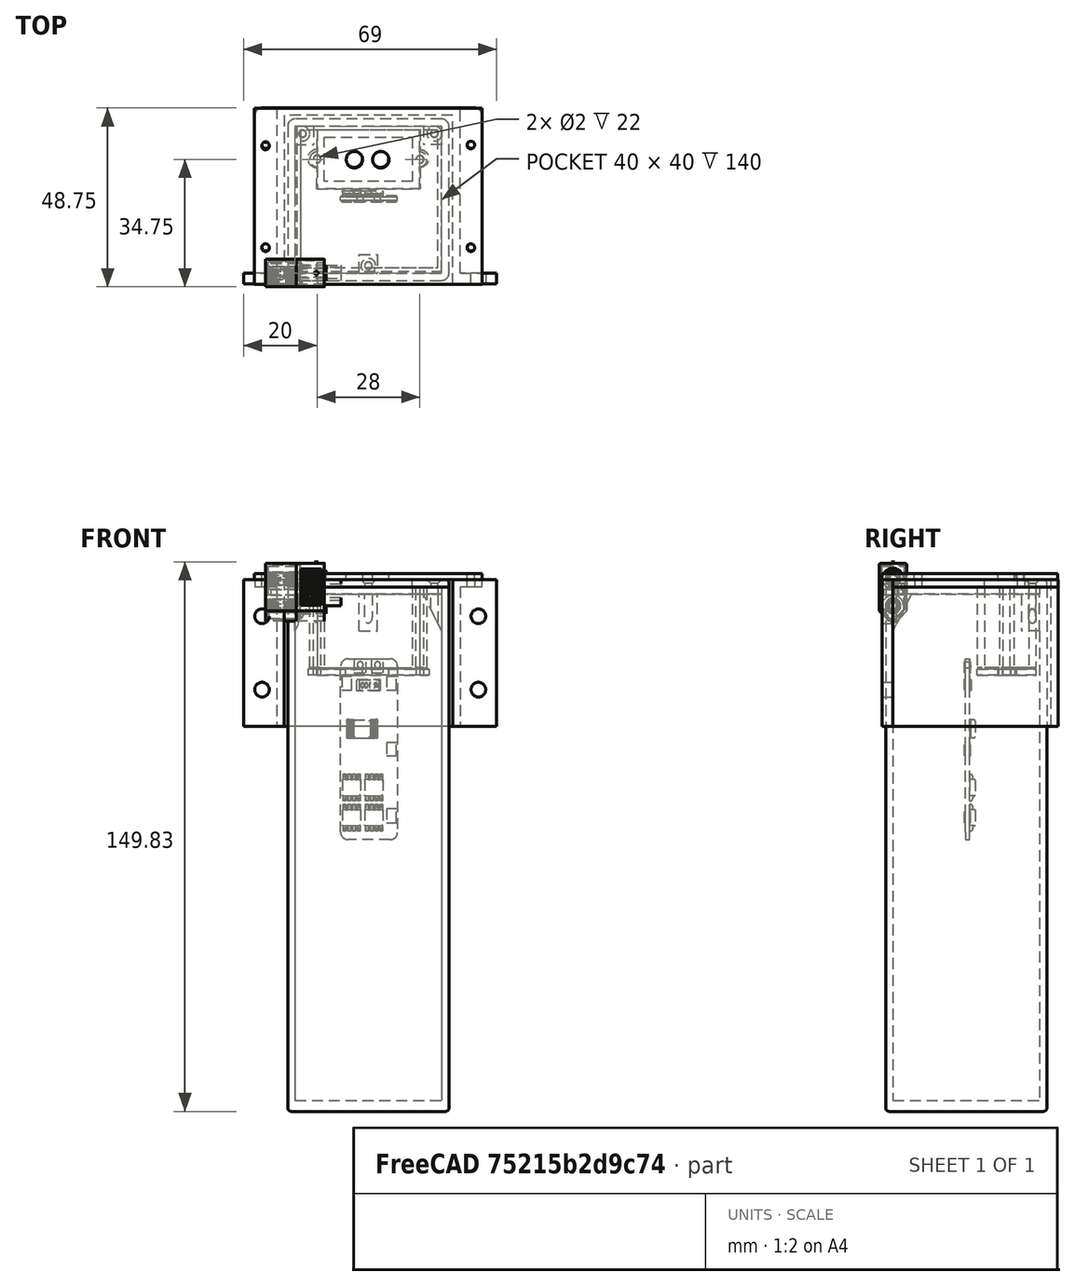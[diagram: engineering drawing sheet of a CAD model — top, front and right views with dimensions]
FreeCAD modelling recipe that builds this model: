
FCSTD DOCUMENT  (FreeCAD 0.20R29177 (Git))
Label: modular_battery_freecad
License: All rights reserved
LicenseURL: http://en.wikipedia.org/wiki/All_rights_reserved
objects: Sketcher::SketchObject×12, Part::Extrusion×11, Part::Feature×9, Part::MultiFuse×7, Mesh::Feature×6, Part::Fillet×3, App::DocumentObjectGroup×3, Part::Compound2×2, Part::Cut×1, Part::Chamfer×1
note: 44 computed .brp shape members not serialized (recipe doc carries the construction recipe); baked Part::Feature solids carry a one-line shape summary decoded from their .brp

FEATURE [Sketcher::SketchObject] Sketch  label="laterales"
  FullyConstrained = true
  sketch-geometry (12):
    g0: LineSegment StartX=0 StartY=0 StartZ=0 EndX=40 EndY=0 EndZ=0
    g1: LineSegment StartX=40 StartY=0 StartZ=0 EndX=40 EndY=40 EndZ=0
    g2: LineSegment StartX=40 StartY=40 StartZ=0 EndX=0 EndY=40 EndZ=0
    g3: LineSegment StartX=0 StartY=40 StartZ=0 EndX=0 EndY=0 EndZ=0
    g4: LineSegment StartX=-4e-16 StartY=-2 StartZ=0 EndX=40 EndY=-2 EndZ=0
    g5: LineSegment StartX=42 StartY=-5e-16 StartZ=0 EndX=42 EndY=40 EndZ=0
    g6: LineSegment StartX=40 StartY=42 StartZ=0 EndX=0 EndY=42 EndZ=0
    g7: LineSegment StartX=-2 StartY=40 StartZ=0 EndX=-2 EndY=0 EndZ=0
    g8: ArcOfCircle CenterX=40 CenterY=40 CenterZ=0 NormalX=0 NormalY=0 NormalZ=1 AngleXU=0 Radius=2 StartAngle=-9e-16 EndAngle=1.5708
    g9: ArcOfCircle CenterX=0 CenterY=40 CenterZ=0 NormalX=0 NormalY=0 NormalZ=1 AngleXU=0 Radius=2 StartAngle=1.5708 EndAngle=3.14159
    g10: ArcOfCircle CenterX=0 CenterY=0 CenterZ=0 NormalX=0 NormalY=0 NormalZ=1 AngleXU=0 Radius=2 StartAngle=3.14159 EndAngle=4.71239
    g11: ArcOfCircle CenterX=40 CenterY=0 CenterZ=0 NormalX=0 NormalY=0 NormalZ=1 AngleXU=0 Radius=2 StartAngle=4.71239 EndAngle=6.28319
  constraints (28):
    c: Coincident(g0,g1)
    c: Coincident(g1,g2)
    c: Coincident(g2,g3)
    c: Coincident(g3,g0)
    c: Horizontal(g0)
    c: Horizontal(g2)
    c: Vertical(g1)
    c: Vertical(g3)
    c: Coincident(g0,g-1)
    c: DistanceX(g2,g2) = 40
    c: DistanceY(g3,g3) = 40
    c: Horizontal(g4)
    c: Horizontal(g6)
    c: Vertical(g5)
    c: Vertical(g7)
    c: Tangent(g5,g8) = -1.5708
    c: Tangent(g6,g8) = -1.5708
    c: Radius(g8) = 2
    c: DistanceX(g1,g5) = 2
    c: Tangent(g6,g9) = -1.5708
    c: Tangent(g7,g9) = -1.5708
    c: Tangent(g4,g10) = -1.5708
    c: Tangent(g7,g10) = -1.5708
    c: Tangent(g4,g11) = -1.5708
    c: Tangent(g5,g11) = -1.5708
    c: Coincident(g11,g0)
    c: Coincident(g10,g0)
    c: Coincident(g2,g9)
FEATURE [Mesh::Feature] _8650_Refrence_Cell  label="18650_Refrence_Cell"
  Placement = pos=(270.809,20.8001,-137.861) rot=(0,0,1;0rad)
FEATURE [Mesh::Feature] _8650_Refrence_Cell001  label="18650_Refrence_Cell001"
  Placement = pos=(249.245,20.7563,-137.861) rot=(0,0,1;0rad)
FEATURE [Mesh::Feature] _8650_Refrence_Cell002  label="18650_Refrence_Cell002"
  Placement = pos=(270.809,-0.622475,-137.861) rot=(0,0,1;0rad)
FEATURE [Mesh::Feature] _8650_Refrence_Cell003  label="18650_Refrence_Cell003"
  Placement = pos=(249.245,-0.66626,-137.861) rot=(0,0,1;0rad)
FEATURE [Mesh::Feature] _8650_Refrence_Cell004  label="18650_Refrence_Cell004"
  Placement = pos=(270.809,-0.622475,-71.3701) rot=(0,0,1;0rad)
FEATURE [Mesh::Feature] _8650_Refrence_Cell005  label="18650_Refrence_Cell005"
  Placement = pos=(249.245,-0.66626,-71.3701) rot=(0,0,1;0rad)
FEATURE [Part::Feature] Solid
  shape: bbox 19.85 x 5.084 x 5.084 mm, 17 faces (baked)
FEATURE [Part::Feature] Solid001
  shape: bbox 19.85 x 5.084 x 5.084 mm, 17 faces (baked)
FEATURE [Part::Feature] Solid002
  shape: bbox 15.7 x 7.5 x 16.55 mm, 359 faces (baked)
FEATURE [Part::Compound2] Compound  label="XT60MaleConnector"
  Links = -> [Solid,Solid001,Solid002]
  Placement = pos=(21.25,31.08,-13.9) rot=(0,1,0;1.5708rad)
FEATURE [Part::Feature] Solid003  label="3PCS BMS Charger Module 12V 10A 18650 Lithium Battery"
  Placement = pos=(20.2003,19.7527,-44.2521) rot=(0,1,0;1.5708rad)
  shape: bbox 15.5 x 2.96 x 49.3 mm, 384 faces (baked)
FEATURE [Part::Extrusion] Extrude  label="laterales001"
  Base = -> Sketch
  Dir = (0,0,1)
  DirMode = 2
  FaceMakerClass = Part::FaceMakerBullseye
  LengthFwd = -140
  LengthRev = 0
  Solid = true
  Symmetric = false
FEATURE [Sketcher::SketchObject] Sketch001  label="base"
  FullyConstrained = true
  Placement = pos=(0,0,-140) rot=(0,0,1;0rad)
  sketch-geometry (8):
    g0: LineSegment StartX=-4e-16 StartY=-2 StartZ=0 EndX=40 EndY=-2 EndZ=0
    g1: LineSegment StartX=42 StartY=-5e-16 StartZ=0 EndX=42 EndY=40 EndZ=0
    g2: LineSegment StartX=40 StartY=42 StartZ=0 EndX=0 EndY=42 EndZ=0
    g3: LineSegment StartX=-2 StartY=40 StartZ=0 EndX=-2 EndY=0 EndZ=0
    g4: ArcOfCircle CenterX=40 CenterY=40 CenterZ=0 NormalX=0 NormalY=0 NormalZ=1 AngleXU=0 Radius=2 StartAngle=-9e-16 EndAngle=1.5708
    g5: ArcOfCircle CenterX=0 CenterY=40 CenterZ=0 NormalX=0 NormalY=0 NormalZ=1 AngleXU=0 Radius=2 StartAngle=1.5708 EndAngle=3.14159
    g6: ArcOfCircle CenterX=0 CenterY=0 CenterZ=0 NormalX=0 NormalY=0 NormalZ=1 AngleXU=0 Radius=2 StartAngle=3.14159 EndAngle=4.71239
    g7: ArcOfCircle CenterX=40 CenterY=0 CenterZ=0 NormalX=0 NormalY=0 NormalZ=1 AngleXU=0 Radius=2 StartAngle=4.71239 EndAngle=6.28319
  constraints (19):
    c: Horizontal(g0)
    c: Horizontal(g2)
    c: Vertical(g1)
    c: Vertical(g3)
    c: Tangent(g1,g4) = -1.5708
    c: Tangent(g2,g4) = -1.5708
    c: Radius(g4) = 2
    c: Tangent(g2,g5) = -1.5708
    c: Tangent(g3,g5) = -1.5708
    c: Tangent(g0,g6) = -1.5708
    c: Tangent(g3,g6) = -1.5708
    c: Tangent(g0,g7) = -1.5708
    c: Tangent(g1,g7) = -1.5708
    c: Radius(g5) = 2
    c: Radius(g7) = 2
    c: Radius(g6) = 2
    c: DistanceX(g2,g2) = 40
    c: DistanceY(g0,g2) = 44
    c: Coincident(g6,g-1)
FEATURE [Part::Extrusion] Extrude001
  Base = -> Sketch001
  Dir = (0,0,1)
  DirMode = 2
  FaceMakerClass = Part::FaceMakerBullseye
  LengthFwd = -3
  LengthRev = 0
  Solid = true
  Symmetric = false
FEATURE [Part::Fillet] Fillet
  Base = -> Extrude001
  Edges = 3 edges r=1: [Edge16,Edge19,Edge22]
FEATURE [Sketcher::SketchObject] Sketch003  label="base002"
  FullyConstrained = true
  sketch-geometry (15):
    g0: LineSegment StartX=-4e-16 StartY=-2 StartZ=0 EndX=40 EndY=-2 EndZ=0
    g1: LineSegment StartX=42 StartY=3.4e-15 StartZ=0 EndX=42 EndY=40 EndZ=0
    g2: LineSegment StartX=40 StartY=42 StartZ=0 EndX=0 EndY=42 EndZ=0
    g3: LineSegment StartX=-2 StartY=40 StartZ=0 EndX=-2 EndY=0 EndZ=0
    g4: ArcOfCircle CenterX=40 CenterY=40 CenterZ=0 NormalX=0 NormalY=0 NormalZ=1 AngleXU=0 Radius=2 StartAngle=-9e-16 EndAngle=1.5708
    g5: ArcOfCircle CenterX=0 CenterY=40 CenterZ=0 NormalX=0 NormalY=0 NormalZ=1 AngleXU=0 Radius=2 StartAngle=1.5708 EndAngle=3.14159
    g6: ArcOfCircle CenterX=0 CenterY=0 CenterZ=0 NormalX=0 NormalY=0 NormalZ=1 AngleXU=0 Radius=2 StartAngle=3.14159 EndAngle=4.71239
    g7: ArcOfCircle CenterX=40 CenterY=3.9e-15 CenterZ=0 NormalX=0 NormalY=0 NormalZ=1 AngleXU=0 Radius=2 StartAngle=4.71239 EndAngle=6.28319
    g8: Circle CenterX=2 CenterY=38 CenterZ=0 NormalX=0 NormalY=0 NormalZ=1 AngleXU=0 Radius=1
    g9: Circle CenterX=38 CenterY=38 CenterZ=0 NormalX=0 NormalY=0 NormalZ=1 AngleXU=0 Radius=1
    g10: Circle CenterX=20 CenterY=2 CenterZ=0 NormalX=0 NormalY=0 NormalZ=1 AngleXU=0 Radius=1
    g11: LineSegment StartX=8 StartY=37 StartZ=0 EndX=32 EndY=37 EndZ=0
    g12: LineSegment StartX=32 StartY=37 StartZ=0 EndX=32 EndY=25 EndZ=0
    g13: LineSegment StartX=32 StartY=25 StartZ=0 EndX=8 EndY=25 EndZ=0
    g14: LineSegment StartX=8 StartY=25 StartZ=0 EndX=8 EndY=37 EndZ=0
  constraints (40):
    c: Horizontal(g0)
    c: Horizontal(g2)
    c: Vertical(g1)
    c: Vertical(g3)
    c: Tangent(g1,g4) = -1.5708
    c: Tangent(g2,g4) = -1.5708
    c: Radius(g4) = 2
    c: Tangent(g2,g5) = -1.5708
    c: Tangent(g3,g5) = -1.5708
    c: Tangent(g0,g6) = -1.5708
    c: Tangent(g3,g6) = -1.5708
    c: Tangent(g0,g7) = -1.5708
    c: Tangent(g1,g7) = -1.5708
    c: Diameter(g8) = 2
    c: Equal(g10,g9)
    c: Equal(g9,g8)
    c: DistanceY(g7,g10) = 2
    c: DistanceX(g10,g7) = 20
    c: DistanceY(g8,g5) = 2
    c: DistanceX(g5,g8) = 2
    c: Radius(g5) = 2
    c: DistanceX(g9,g4) = 2
    c: DistanceY(g9,g4) = 2
    c: Radius(g7) = 2
    c: Radius(g6) = 2
    c: DistanceX(g2,g2) = 40
    c: DistanceY(g0,g2) = 44
    c: Coincident(g6,g-1)
    c: Coincident(g11,g12)
    c: Coincident(g12,g13)
    c: Coincident(g13,g14)
    c: Coincident(g14,g11)
    c: Horizontal(g11)
    c: Horizontal(g13)
    c: Vertical(g12)
    c: Vertical(g14)
    c: DistanceX(g11,g1) = 10
    c: DistanceX(g3,g11) = 10
    c: DistanceY(g11,g2) = 5
    c: DistanceY(g0,g12) = 27
FEATURE [Sketcher::SketchObject] Sketch004  label="base003"
  FullyConstrained = false
  sketch-geometry (14):
    g0: LineSegment StartX=8 StartY=37 StartZ=0 EndX=32 EndY=37 EndZ=0
    g1: LineSegment StartX=32 StartY=37 StartZ=0 EndX=32 EndY=25 EndZ=0
    g2: LineSegment StartX=32 StartY=25 StartZ=0 EndX=8 EndY=25 EndZ=0
    g3: LineSegment StartX=8 StartY=25 StartZ=0 EndX=8 EndY=37 EndZ=0
    g4: LineSegment StartX=34 StartY=39 StartZ=0 EndX=6 EndY=39 EndZ=0
    g5: LineSegment StartX=6 StartY=39 StartZ=0 EndX=6 EndY=33 EndZ=0
    g6: LineSegment StartX=6 StartY=23 StartZ=0 EndX=34 EndY=23 EndZ=0
    g7: LineSegment StartX=34 StartY=23 StartZ=0 EndX=34 EndY=29 EndZ=0
    g8: Circle CenterX=6 CenterY=31 CenterZ=0 NormalX=0 NormalY=0 NormalZ=1 AngleXU=0 Radius=1
    g9: ArcOfCircle CenterX=6 CenterY=31 CenterZ=0 NormalX=0 NormalY=0 NormalZ=1 AngleXU=0 Radius=2 StartAngle=1.5708 EndAngle=4.71239
    g10: LineSegment StartX=6 StartY=29 StartZ=0 EndX=6 EndY=23 EndZ=0
    g11: Circle CenterX=34 CenterY=31 CenterZ=0 NormalX=0 NormalY=0 NormalZ=1 AngleXU=0 Radius=1
    g12: ArcOfCircle CenterX=34 CenterY=31 CenterZ=0 NormalX=0 NormalY=0 NormalZ=1 AngleXU=0 Radius=2 StartAngle=4.71239 EndAngle=7.85398
    g13: LineSegment StartX=34 StartY=33 StartZ=0 EndX=34 EndY=39 EndZ=0
  constraints (42):
    c: Coincident(g0,g1)
    c: Coincident(g1,g2)
    c: Coincident(g2,g3)
    c: Coincident(g3,g0)
    c: Horizontal(g0)
    c: Horizontal(g2)
    c: Vertical(g1)
    c: Vertical(g3)
    c: DistanceY(g-1,g2) = 25
    c: DistanceX(g-1,g2) = 8
    c: DistanceX(g0,g0) = 24
    c: DistanceY(g1,g1) = 12
    c: Coincident(g4,g5)
    c: Coincident(g10,g6)
    c: Coincident(g6,g7)
    c: Coincident(g13,g4)
    c: Horizontal(g4)
    c: Horizontal(g6)
    c: Vertical(g5)
    c: Vertical(g7)
    c: DistanceY(g10,g2) = 2
    c: DistanceX(g10,g2) = 2
    c: DistanceX(g6,g6) = 28
    c: PointOnObject(g8,g5)
    c: Coincident(g9,g8)
    c: Diameter(g8) = 2
    c: Diameter(g9) = 4
    c: Coincident(g5,g9)
    c: Coincident(g9,g10)
    c: PointOnObject(g11,g7)
    c: Coincident(g12,g11)
    c: Diameter(g11) = 2
    c: Diameter(g12) = 4
    c: PointOnObject(g12,g7)
    c: Coincident(g7,g12)
    c: PointOnObject(g13,g12)
    c: DistanceY(g6,g4) = 16
    c: Vertical(g13)
    c: DistanceY(g6,g11) = 8
    c: DistanceY(g6,g8) = 8
    c: Vertical(g10)
    c: DistanceX(g5,g0) = 2
FEATURE [Sketcher::SketchObject] Sketch005  label="base004"
  FullyConstrained = true
  sketch-geometry (8):
    g0: LineSegment StartX=8 StartY=37 StartZ=0 EndX=32 EndY=37 EndZ=0
    g1: LineSegment StartX=32 StartY=37 StartZ=0 EndX=32 EndY=25 EndZ=0
    g2: LineSegment StartX=32 StartY=25 StartZ=0 EndX=8 EndY=25 EndZ=0
    g3: LineSegment StartX=8 StartY=25 StartZ=0 EndX=8 EndY=37 EndZ=0
    g4: LineSegment StartX=6 StartY=39 StartZ=0 EndX=34 EndY=39 EndZ=0
    g5: LineSegment StartX=34 StartY=39 StartZ=0 EndX=34 EndY=23 EndZ=0
    g6: LineSegment StartX=34 StartY=23 StartZ=0 EndX=6 EndY=23 EndZ=0
    g7: LineSegment StartX=6 StartY=23 StartZ=0 EndX=6 EndY=39 EndZ=0
  constraints (24):
    c: Coincident(g0,g1)
    c: Coincident(g1,g2)
    c: Coincident(g2,g3)
    c: Coincident(g3,g0)
    c: Horizontal(g0)
    c: Horizontal(g2)
    c: Vertical(g1)
    c: Vertical(g3)
    c: DistanceY(g-1,g2) = 25
    c: DistanceX(g-1,g2) = 8
    c: DistanceX(g0,g0) = 24
    c: DistanceY(g1,g1) = 12
    c: Coincident(g4,g5)
    c: Coincident(g5,g6)
    c: Coincident(g6,g7)
    c: Coincident(g7,g4)
    c: Horizontal(g4)
    c: Horizontal(g6)
    c: Vertical(g5)
    c: Vertical(g7)
    c: DistanceX(g1,g5) = 2
    c: DistanceY(g5,g1) = 2
    c: DistanceY(g5,g5) = 16
    c: DistanceX(g4,g4) = 28
FEATURE [Part::Extrusion] Extrude002
  Base = -> Sketch003
  Dir = (0,0,1)
  DirMode = 2
  FaceMakerClass = Part::FaceMakerBullseye
  LengthFwd = 2
  LengthRev = 0
  Solid = true
  Symmetric = false
FEATURE [Part::Extrusion] Extrude003
  Base = -> Sketch004
  Dir = (0,0,1)
  DirMode = 2
  FaceMakerClass = Part::FaceMakerBullseye
  LengthFwd = -22
  LengthRev = 0
  Solid = true
  Symmetric = false
FEATURE [Part::Feature] Solid004
  shape: bbox 19.85 x 5.085 x 5.085 mm, 36 faces (baked)
FEATURE [Part::Feature] Solid005
  shape: bbox 19.85 x 5.085 x 5.085 mm, 36 faces (baked)
FEATURE [Part::Feature] Solid006
  shape: bbox 16 x 7.5 x 16.55 mm, 345 faces (baked)
FEATURE [Part::Compound2] Compound001  label="XT60FemaleConnector"
  Links = -> [Solid004,Solid005,Solid006]
  Placement = pos=(21.25,31.04,-6) rot=(0.707107,0,0.707107;3.14159rad)
FEATURE [Part::Fillet] Fillet001
  Base = -> Extrude002
  Edges = 1 edges r=1: [Edge16]
FEATURE [Part::MultiFuse] Fusion
  Shapes = -> [Extrude,Fillet]
FEATURE [Sketcher::SketchObject] Sketch006  label="base005"
  FullyConstrained = true
  sketch-geometry (8):
    g0: LineSegment StartX=0.5 StartY=0.5 StartZ=0 EndX=40 EndY=0.5 EndZ=0
    g1: LineSegment StartX=40 StartY=0.5 StartZ=0 EndX=40 EndY=40 EndZ=0
    g2: LineSegment StartX=40 StartY=40 StartZ=0 EndX=0.5 EndY=40 EndZ=0
    g3: LineSegment StartX=0.5 StartY=40 StartZ=0 EndX=0.5 EndY=0.5 EndZ=0
    g4: LineSegment StartX=39 StartY=39 StartZ=0 EndX=1.5 EndY=39 EndZ=0
    g5: LineSegment StartX=1.5 StartY=39 StartZ=0 EndX=1.5 EndY=1.5 EndZ=0
    g6: LineSegment StartX=1.5 StartY=1.5 StartZ=0 EndX=39 EndY=1.5 EndZ=0
    g7: LineSegment StartX=39 StartY=1.5 StartZ=0 EndX=39 EndY=39 EndZ=0
  constraints (24):
    c: Coincident(g0,g1)
    c: Coincident(g1,g2)
    c: Coincident(g2,g3)
    c: Horizontal(g0)
    c: Horizontal(g2)
    c: Vertical(g1)
    c: Vertical(g3)
    c: DistanceY(g1,g1) = 39.5
    c: DistanceX(g0,g0) = 39.5
    c: Coincident(g0,g3)
    c: DistanceX(g-1,g0) = 0.5
    c: DistanceY(g-1,g0) = 0.5
    c: Coincident(g4,g5)
    c: Coincident(g5,g6)
    c: Coincident(g6,g7)
    c: Coincident(g7,g4)
    c: Horizontal(g4)
    c: Horizontal(g6)
    c: Vertical(g5)
    c: Vertical(g7)
    c: DistanceY(g4,g1) = 1
    c: DistanceX(g4,g1) = 1
    c: DistanceX(g4,g4) = 37.5
    c: DistanceY(g7,g7) = 37.5
FEATURE [Part::Extrusion] Extrude004
  Base = -> Sketch006
  Dir = (0,0,1)
  DirMode = 2
  FaceMakerClass = Part::FaceMakerBullseye
  LengthFwd = -2
  LengthRev = 0
  Solid = true
  Symmetric = false
FEATURE [Part::MultiFuse] Fusion001
  Shapes = -> [Fillet001,Extrude004]
FEATURE [Part::MultiFuse] Fusion002
  Shapes = -> [Fusion001,Extrude003]
FEATURE [Sketcher::SketchObject] Sketch008  label="base006"
  FullyConstrained = false
  sketch-geometry (3):
    g0: Circle CenterX=2 CenterY=38 CenterZ=0 NormalX=0 NormalY=0 NormalZ=1 AngleXU=0 Radius=1
    g1: Circle CenterX=38 CenterY=38 CenterZ=0 NormalX=0 NormalY=0 NormalZ=1 AngleXU=0 Radius=1
    g2: Circle CenterX=20 CenterY=2 CenterZ=0 NormalX=0 NormalY=0 NormalZ=1 AngleXU=0 Radius=1
  constraints (2):
    c: Diameter(g0) = 2
    c: Equal(g2,g1)
FEATURE [Sketcher::SketchObject] Sketch007  label="laterales002"
  FullyConstrained = true
  Placement = pos=(0,0,2) rot=(0,0,1;0rad)
  sketch-geometry (8):
    g0: LineSegment StartX=43 StartY=-3 StartZ=0 EndX=43 EndY=43 EndZ=0
    g1: LineSegment StartX=43 StartY=43 StartZ=0 EndX=-3 EndY=43 EndZ=0
    g2: LineSegment StartX=-3 StartY=43 StartZ=0 EndX=-3 EndY=-3 EndZ=0
    g3: LineSegment StartX=45 StartY=-3 StartZ=0 EndX=45 EndY=45 EndZ=0
    g4: LineSegment StartX=45 StartY=45 StartZ=0 EndX=-5 EndY=45 EndZ=0
    g5: LineSegment StartX=-5 StartY=45 StartZ=0 EndX=-5 EndY=-3 EndZ=0
    g6: LineSegment StartX=45 StartY=-3 StartZ=0 EndX=43 EndY=-3 EndZ=0
    g7: LineSegment StartX=-3 StartY=-3 StartZ=0 EndX=-5 EndY=-3 EndZ=0
  constraints (24):
    c: Coincident(g0,g1)
    c: Coincident(g1,g2)
    c: Horizontal(g1)
    c: Vertical(g0)
    c: Vertical(g2)
    c: DistanceX(g1,g1) = 46
    c: DistanceY(g0,g0) = 46
    c: DistanceY(g2,g-1) = 3
    c: DistanceX(g2,g-1) = 3
    c: Coincident(g3,g4)
    c: Coincident(g4,g5)
    c: Horizontal(g4)
    c: Vertical(g3)
    c: Vertical(g5)
    c: DistanceY(g3,g3) = 48
    c: DistanceX(g4,g4) = 50
    c: DistanceY(g1,g4) = 2
    c: Coincident(g6,g3)
    c: Coincident(g6,g0)
    c: DistanceY(g5,g5) = 48
    c: Coincident(g7,g2)
    c: Horizontal(g7)
    c: Coincident(g5,g7)
    c: DistanceX(g7,g7) = 2
FEATURE [Sketcher::SketchObject] Sketch009
  FullyConstrained = true
  Placement = pos=(0,40,0) rot=(1,0,0;1.5708rad)
  sketch-geometry (6):
    g0: LineSegment StartX=0 StartY=0 StartZ=0 EndX=5 EndY=0 EndZ=0
    g1: LineSegment StartX=5 StartY=0 StartZ=0 EndX=0 EndY=-10 EndZ=0
    g2: LineSegment StartX=0 StartY=-10 StartZ=0 EndX=0 EndY=0 EndZ=0
    g3: LineSegment StartX=40 StartY=0 StartZ=0 EndX=35 EndY=0 EndZ=0
    g4: LineSegment StartX=40 StartY=0 StartZ=0 EndX=40 EndY=-10 EndZ=0
    g5: LineSegment StartX=40 StartY=-10 StartZ=0 EndX=35 EndY=0 EndZ=0
  constraints (17):
    c: Coincident(g0,g-1)
    c: Horizontal(g0)
    c: Coincident(g1,g0)
    c: PointOnObject(g1,g-2)
    c: Coincident(g2,g1)
    c: Coincident(g2,g0)
    c: DistanceY(g2,g2) = 10
    c: DistanceX(g0,g0) = 5
    c: PointOnObject(g3,g-1)
    c: PointOnObject(g3,g-1)
    c: DistanceX(g0,g3) = 40
    c: DistanceX(g3,g3) = 5
    c: Coincident(g4,g3)
    c: Vertical(g4)
    c: Coincident(g5,g4)
    c: Coincident(g5,g3)
    c: DistanceY(g4,g4) = 10
FEATURE [Part::Extrusion] Extrude005
  Base = -> Sketch009
  Dir = (0,-1,2e-16)
  DirMode = 2
  FaceMakerClass = Part::FaceMakerBullseye
  LengthFwd = 5
  LengthRev = 0
  Solid = true
  Symmetric = false
FEATURE [Sketcher::SketchObject] Sketch010
  FullyConstrained = true
  Placement = pos=(17.5,0,0) rot=(0.57735,0.57735,0.57735;2.0944rad)
  sketch-geometry (3):
    g0: LineSegment StartX=0 StartY=0 StartZ=0 EndX=5 EndY=0 EndZ=0
    g1: LineSegment StartX=5 StartY=0 StartZ=0 EndX=0 EndY=-10 EndZ=0
    g2: LineSegment StartX=0 StartY=-10 StartZ=0 EndX=0 EndY=0 EndZ=0
  constraints (8):
    c: Coincident(g0,g-1)
    c: PointOnObject(g0,g-1)
    c: Coincident(g1,g0)
    c: PointOnObject(g1,g-2)
    c: Coincident(g2,g1)
    c: Coincident(g2,g0)
    c: DistanceX(g0,g0) = 5
    c: DistanceY(g2,g2) = 10
FEATURE [Part::Extrusion] Extrude006
  Base = -> Sketch010
  Dir = (1,-2e-16,2e-16)
  DirMode = 2
  FaceMakerClass = Part::FaceMakerBullseye
  LengthFwd = 5
  LengthRev = 0
  Solid = true
  Symmetric = false
FEATURE [Part::Extrusion] Extrude007
  Base = -> Sketch008
  Dir = (0,0,1)
  DirMode = 2
  FaceMakerClass = Part::FaceMakerBullseye
  LengthFwd = -10
  LengthRev = 0
  Solid = true
  Symmetric = false
FEATURE [Part::MultiFuse] Fusion003
  Shapes = -> [Extrude005,Extrude006]
FEATURE [Part::Cut] Cut
  Base = -> Fusion003
  Placement = pos=(0,0,-2) rot=(0,0,1;0rad)
  Tool = -> Extrude007
FEATURE [Part::Chamfer] Chamfer
  Base = -> Fusion002
  Edges = 3 edges r=1: [Edge96,Edge98,Edge100]
FEATURE [Part::MultiFuse] Fusion004
  Shapes = -> [Cut,Fusion]
FEATURE [Part::Feature] Solid009  label="modular_battery_kicad 1"
  Placement = pos=(6.11,23.06,-24) rot=(0,0,1;0rad)
  shape: bbox 32.96 x 16.2 x 1.6 mm, 15 faces (baked)
FEATURE [App::DocumentObjectGroup] Group  label="vitamins"
  Group = -> [_8650_Refrence_Cell,_8650_Refrence_Cell001,_8650_Refrence_Cell002,_8650_Refrence_Cell003,_8650_Refrence_Cell004,_8650_Refrence_Cell005,Compound,Solid003,Solid009]
FEATURE [Part::Extrusion] Extrude008
  Base = -> Sketch007
  Dir = (0,0,1)
  DirMode = 2
  FaceMakerClass = Part::FaceMakerBullseye
  LengthFwd = -40
  LengthRev = 0
  Solid = true
  Symmetric = false
FEATURE [Sketcher::SketchObject] Sketch011  label="laterales003"
  FullyConstrained = true
  Placement = pos=(0,0,2) rot=(0,0,1;0rad)
  sketch-geometry (12):
    g0: LineSegment StartX=45 StartY=-3 StartZ=0 EndX=51 EndY=-3 EndZ=0
    g1: LineSegment StartX=51 StartY=-3 StartZ=0 EndX=51 EndY=45 EndZ=0
    g2: LineSegment StartX=51 StartY=45 StartZ=0 EndX=45 EndY=45 EndZ=0
    g3: LineSegment StartX=45 StartY=45 StartZ=0 EndX=45 EndY=-3 EndZ=0
    g4: LineSegment StartX=-5 StartY=45 StartZ=0 EndX=-11 EndY=45 EndZ=0
    g5: LineSegment StartX=-11 StartY=45 StartZ=0 EndX=-11 EndY=-3 EndZ=0
    g6: LineSegment StartX=-11 StartY=-3 StartZ=0 EndX=-5 EndY=-3 EndZ=0
    g7: LineSegment StartX=-5 StartY=-3 StartZ=0 EndX=-5 EndY=45 EndZ=0
    g8: Circle CenterX=48 CenterY=35 CenterZ=0 NormalX=0 NormalY=0 NormalZ=1 AngleXU=0 Radius=1
    g9: Circle CenterX=48 CenterY=7 CenterZ=0 NormalX=0 NormalY=0 NormalZ=1 AngleXU=0 Radius=1
    g10: Circle CenterX=-8 CenterY=7 CenterZ=0 NormalX=0 NormalY=0 NormalZ=1 AngleXU=0 Radius=1
    g11: Circle CenterX=-8 CenterY=35 CenterZ=0 NormalX=0 NormalY=0 NormalZ=1 AngleXU=0 Radius=1
  constraints (36):
    c: DistanceY(g0,g2) = 48
    c: DistanceX(g4,g2) = 50
    c: DistanceY(g6,g4) = 48
    c: Coincident(g0,g1)
    c: Coincident(g1,g2)
    c: Coincident(g2,g3)
    c: Coincident(g3,g0)
    c: Horizontal(g0)
    c: Horizontal(g2)
    c: Vertical(g1)
    c: DistanceX(g2,g2) = 6
    c: DistanceY(g-1,g2) = 45
    c: DistanceX(g6,g-1) = 5
    c: DistanceY(g6,g-1) = 3
    c: Coincident(g4,g5)
    c: Coincident(g5,g6)
    c: Coincident(g6,g7)
    c: Coincident(g7,g4)
    c: Horizontal(g4)
    c: Horizontal(g6)
    c: Vertical(g5)
    c: DistanceX(g4,g4) = 6
    c: Equal(g10,g11)
    c: Equal(g11,g8)
    c: Equal(g8,g9)
    c: Diameter(g9) = 2
    c: DistanceX(g0,g9) = 3
    c: DistanceY(g0,g9) = 10
    c: DistanceX(g0,g8) = 3
    c: DistanceY(g8,g2) = 10
    c: DistanceX(g11,g4) = 3
    c: DistanceY(g11,g4) = 10
    c: DistanceX(g10,g6) = 3
    c: DistanceY(g6,g10) = 10
    c: DistanceX(g6,g6) = 6
    c: DistanceX(g0,g0) = 6
FEATURE [Part::Extrusion] Extrude009
  Base = -> Sketch011
  Dir = (0,0,1)
  DirMode = 2
  FaceMakerClass = Part::FaceMakerBullseye
  LengthFwd = -2
  LengthRev = 0
  Solid = true
  Symmetric = false
FEATURE [Sketcher::SketchObject] Sketch012
  FullyConstrained = true
  Placement = pos=(0,0,0) rot=(1,0,0;1.5708rad)
  sketch-geometry (12):
    g0: LineSegment StartX=-4 StartY=2 StartZ=0 EndX=-14 EndY=2 EndZ=0
    g1: LineSegment StartX=-14 StartY=2 StartZ=0 EndX=-14 EndY=-38 EndZ=0
    g2: LineSegment StartX=-14 StartY=-38 StartZ=0 EndX=-4 EndY=-38 EndZ=0
    g3: LineSegment StartX=-4 StartY=-38 StartZ=0 EndX=-4 EndY=2 EndZ=0
    g4: LineSegment StartX=55 StartY=2 StartZ=0 EndX=45 EndY=2 EndZ=0
    g5: LineSegment StartX=45 StartY=2 StartZ=0 EndX=45 EndY=-38 EndZ=0
    g6: LineSegment StartX=45 StartY=-38 StartZ=0 EndX=55 EndY=-38 EndZ=0
    g7: LineSegment StartX=55 StartY=-38 StartZ=0 EndX=55 EndY=2 EndZ=0
    g8: Circle CenterX=-9 CenterY=-8 CenterZ=0 NormalX=0 NormalY=0 NormalZ=1 AngleXU=0 Radius=2
    g9: Circle CenterX=-9 CenterY=-28 CenterZ=0 NormalX=0 NormalY=0 NormalZ=1 AngleXU=0 Radius=2
    g10: Circle CenterX=50 CenterY=-8 CenterZ=0 NormalX=0 NormalY=0 NormalZ=1 AngleXU=0 Radius=2
    g11: Circle CenterX=50 CenterY=-28 CenterZ=0 NormalX=0 NormalY=0 NormalZ=1 AngleXU=0 Radius=2
  constraints (36):
    c: Coincident(g0,g1)
    c: Coincident(g1,g2)
    c: Coincident(g2,g3)
    c: Coincident(g3,g0)
    c: Horizontal(g0)
    c: Horizontal(g2)
    c: Vertical(g1)
    c: Vertical(g3)
    c: DistanceX(g2,g2) = 10
    c: DistanceY(g1,g1) = 40
    c: DistanceY(g-1,g0) = 2
    c: DistanceX(g0,g-1) = 4
    c: Coincident(g4,g5)
    c: Coincident(g5,g6)
    c: Coincident(g6,g7)
    c: Coincident(g7,g4)
    c: Horizontal(g4)
    c: Horizontal(g6)
    c: Vertical(g5)
    c: Vertical(g7)
    c: DistanceX(g6,g6) = 10
    c: DistanceY(g7,g7) = 40
    c: DistanceX(g-1,g4) = 45
    c: DistanceY(g-1,g4) = 2
    c: Equal(g11,g10)
    c: Equal(g10,g8)
    c: Equal(g8,g9)
    c: Diameter(g11) = 4
    c: DistanceX(g8,g0) = 5
    c: DistanceX(g9,g2) = 5
    c: DistanceX(g5,g11) = 5
    c: DistanceX(g4,g10) = 5
    c: DistanceY(g10,g4) = 10
    c: DistanceY(g5,g11) = 10
    c: DistanceY(g2,g9) = 10
    c: DistanceY(g8,g0) = 10
FEATURE [Part::Extrusion] Extrude010
  Base = -> Sketch012
  Dir = (0,-1,-3e-16)
  DirMode = 2
  FaceMakerClass = Part::FaceMakerBullseye
  LengthFwd = 3
  LengthRev = 0
  Solid = true
  Symmetric = false
FEATURE [Part::Fillet] Fillet002
  Base = -> Extrude009
  Edges = 2 edges r=2: [Edge2,Edge23]
FEATURE [Part::MultiFuse] Fusion005
  Shapes = -> [Fillet002,Extrude008]
FEATURE [Part::MultiFuse] Fusion006
  Shapes = -> [Fusion005,Extrude010]
FEATURE [Part::Feature] Solid010  label="modular_battery_kicads 1"
  Placement = pos=(-51.8005,27.91,2) rot=(0,0,1;0rad)
  shape: bbox 62 x 48 x 1.6 mm, 12 faces (baked)
FEATURE [App::DocumentObjectGroup] Group001  label="portapilas"
  Group = -> [Fusion004,Chamfer]
FEATURE [App::DocumentObjectGroup] Group002  label="anclaje"
  Group = -> [Fusion006,Solid010,Compound001]
